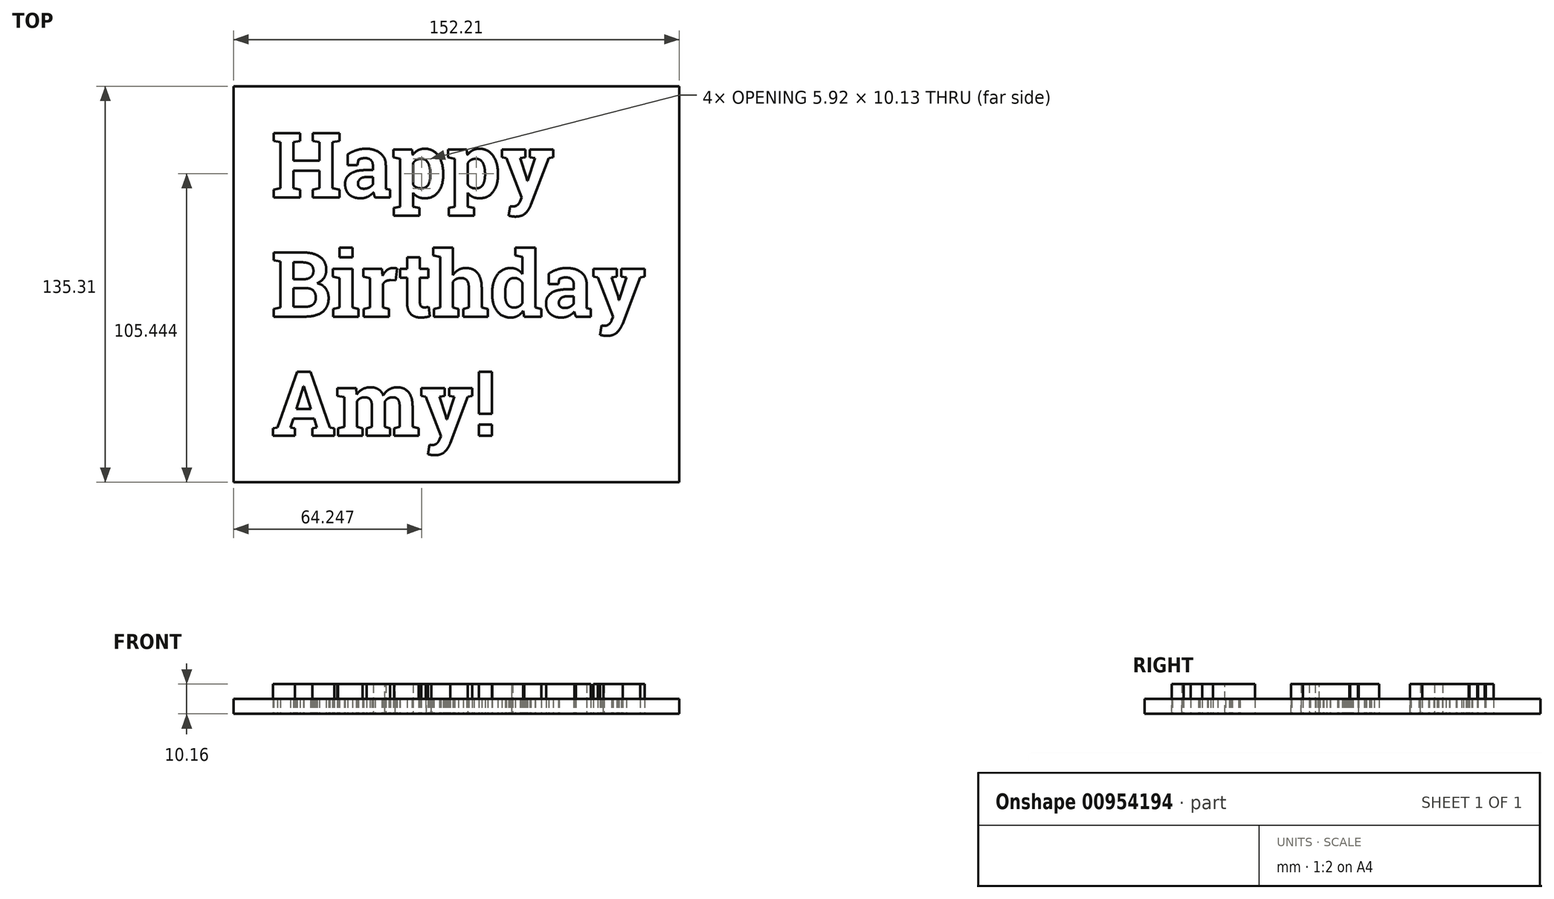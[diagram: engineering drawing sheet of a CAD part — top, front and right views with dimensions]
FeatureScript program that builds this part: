
annotation { "Feature Type Name" : "Feature", "Feature Type Description" : "" }
export const myFeature = defineFeature(function(context is Context, id is Id, definition is map)
    precondition{}
    {
        {
            var Q0;
            Q0=qCreatedBy(makeId("Top.planeOp"),FACE);
            var sketch = newSketch(context, id + "F0", { "sketchPlane" : qUnion([Q0])});
            skText(sketch, "E0", { "text": "Happy\nBirthday\nAmy!", "fontName": "RobotoSlab-Bold.ttf"});
            const initialGuessF0  = {"E0": [-0.06313, 0, 1, 0, 0.02223]};
            skSetInitialGuess(sketch, initialGuessF0);
            skSolve(sketch);
        }
        {
            var Q0;
            Q0=qCreatedBy(makeId("Top.planeOp"),FACE);
            var sketch = newSketch(context, id + "F1", { "sketchPlane" : qUnion([Q0])});
            skLineSegment(sketch, "E1.bottom", {"start": v(-75.96, 38) * mm, "end": v(76.25, 38) * mm});
            skLineSegment(sketch, "E1.top", {"start": v(-75.96, -97.32) * mm, "end": v(76.25, -97.32) * mm});
            skLineSegment(sketch, "E1.left", {"start": v(-75.96, 38) * mm, "end": v(-75.96, -97.32) * mm});
            skLineSegment(sketch, "E1.right", {"start": v(76.25, 38) * mm, "end": v(76.25, -97.32) * mm});
            skSolve(sketch);
        }
        {
            var Q0;
            Q0 = qSketchRegion(id + "F0", true);
            var Q1;
            Q1 = qSketchRegion(id + "F1", true);
            extrude(context, id + "F2", {"entities" : qUnion([Q0, Q1]), "depth" : 5.08 * mm, "offsetDistance" : 25.4 * mm});
        }
        {
            var Q0;
            Q0 = qSketchRegion(id + "F0", true);
            extrude(context, id + "F3", {"entities" : qUnion([Q0]), "depth" : 10.16 * mm, "offsetDistance" : 25.4 * mm});
        }
    });
